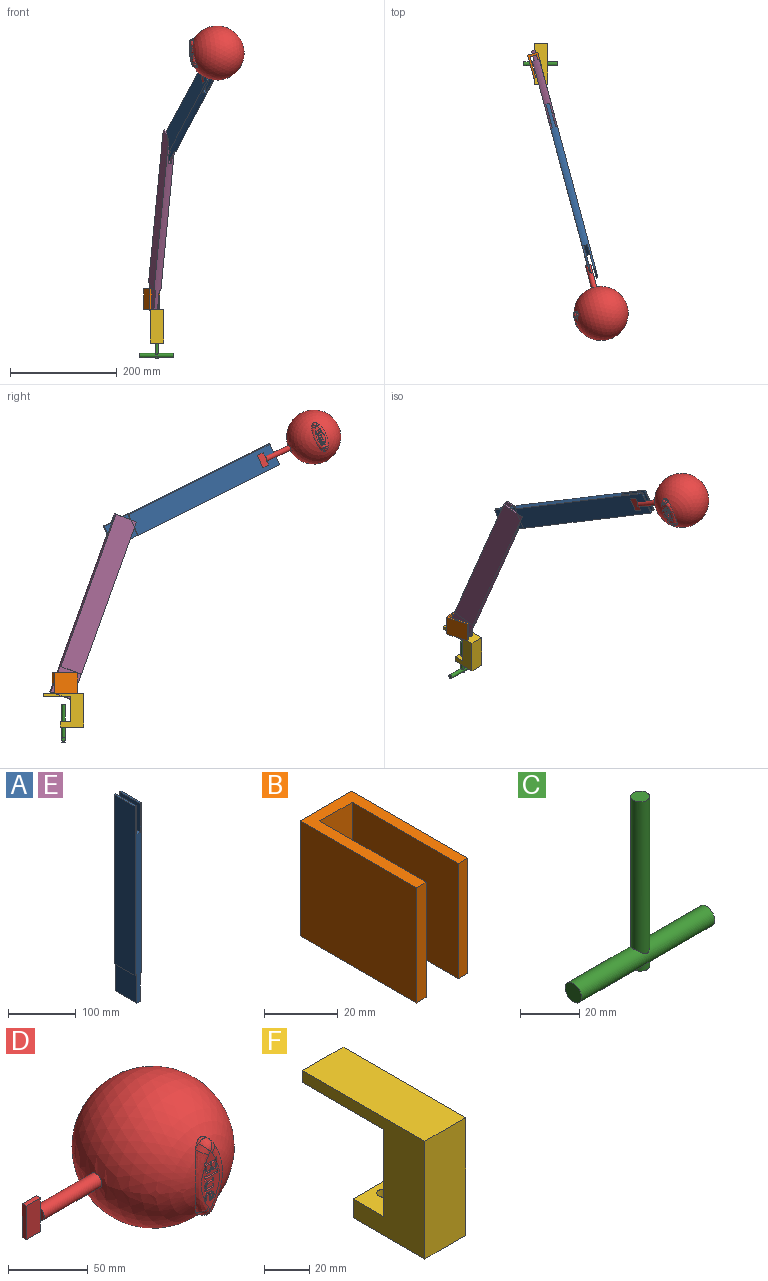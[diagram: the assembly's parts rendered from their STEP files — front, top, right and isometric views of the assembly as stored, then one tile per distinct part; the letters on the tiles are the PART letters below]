
ASSEMBLY  parts=6 mates=5
PART A: 14 faces, bbox 13.3x44.5x355.6 mm
  f0: plane 304.8x42.43mm, normal (-1,0,0), area 12932.3mm2, adj f1,f3,f6,f12
  f1: cylinder r=22.23mm len=355.6mm, axis (0,0,-1), area 4102.5mm2, adj f0,f2,f4,f5,f6,f7,f8,f9
  f2: plane 304.8x42.43mm, normal (1,0,0), area 12931.6mm2, adj f1,f3,f5,f10
  f3: cylinder r=22.23mm len=355.6mm, axis (0,0,-1), area 4102.5mm2, adj f0,f2,f4,f5,f6,f7,f8,f9
  f4: plane 44.45x6.85mm, normal (0,0,-1), area 303.3mm2, adj f1,f3,f11,f13
  f5: plane 43.92x3.2mm, normal (0,0,1), area 138.4mm2, adj f1,f2,f3,f9
  f6: plane 43.92x3.2mm, normal (0,0,1), area 138.5mm2, adj f0,f1,f3,f8
  f7: plane 44.45x6.85mm, normal (0,0,1), area 303.4mm2, adj f1,f3,f8,f9
  f8: plane 50.8x43.92mm, normal (1,0,0), area 2231.1mm2, adj f1,f3,f6,f7
  f9: plane 50.8x43.92mm, normal (-1,0,0), area 2231mm2, adj f1,f3,f5,f7
  f10: plane 43.92x3.2mm, normal (0,0,-1), area 138.6mm2, adj f1,f2,f3,f11
  f11: plane 50.8x43.92mm, normal (1,0,0), area 2231.1mm2, adj f1,f3,f4,f10
  f12: plane 43.92x3.2mm, normal (0,0,-1), area 138.4mm2, adj f0,f1,f3,f13
  f13: plane 50.8x43.92mm, normal (-1,0,0), area 2231.1mm2, adj f1,f3,f4,f12
PART B: 10 faces, bbox 19.8x44.5x38.1 mm
  f0: plane 38.1x3.72mm, normal (0,-1,0), area 141.8mm2, adj f1,f7,f8,f9
  f1: plane 44.45x38.1mm, normal (1,0,0), area 1693.5mm2, adj f0,f2,f8,f9
  f2: plane 38.1x19.78mm, normal (0,1,0), area 753.8mm2, adj f1,f3,f8,f9
  f3: plane 44.45x38.1mm, normal (-1,0,0), area 1693.5mm2, adj f2,f4,f8,f9
  f4: plane 38.1x3.77mm, normal (0,-1,0), area 143.7mm2, adj f3,f5,f8,f9
  f5: plane 40.62x38.1mm, normal (1,0,0), area 1547.5mm2, adj f4,f6,f8,f9
  f6: plane 38.1x12.29mm, normal (0,-1,0), area 468.3mm2, adj f5,f7,f8,f9
  f7: plane 40.62x38.1mm, normal (-1,0,0), area 1547.5mm2, adj f0,f6,f8,f9
  f8: plane 44.45x19.78mm, normal (0,0,1), area 380.2mm2, adj f0,f1,f2,f3,f4,f5,f6,f7
  f9: plane 44.45x19.78mm, normal (0,0,-1), area 380.2mm2, adj f0,f1,f2,f3,f4,f5,f6,f7
PART C: 7 faces, bbox 63.5x7.7x69.9 mm
  f0: cylinder r=3.17mm len=6.35mm, axis (0,0,1), area 33.7mm2, adj f1,f2
  f1: plane 6.35x6.35mm, normal (0,0,-1), area 31.7mm2, adj f0
  f2: cylinder r=3.83mm len=63.5mm, axis (-1,0,0), area 1458.5mm2, adj f0,f3,f4,f6
  f3: plane 7.67x7.67mm, normal (1,0,0), area 46.2mm2, adj f2
  f4: plane 7.67x7.67mm, normal (-1,0,0), area 46.2mm2, adj f2
  f5: plane 6.35x6.35mm, normal (0,0,1), area 31.7mm2, adj f6
  f6: cylinder r=3.17mm len=63.13mm, axis (0,0,1), area 1238.2mm2, adj f2,f5
PART D: 115 faces, bbox 165.2x101.7x101.7 mm
  f0: plane 35.77x16.03mm, normal (0,-1,0), area 275.1mm2, adj f2,f3,f17,f19,f35,f36,f37,f38
  f1: plane 8.58x8.06mm, normal (0,-1,0), area 40.5mm2, adj f2,f3,f20,f22,f47,f48,f50
  f2: bspline ~49.37x11.19mm, area 297mm2, adj f0,f1,f5,f17,f20,f35,f50
  f3: bspline ~49.37x11.19mm, area 294.8mm2, adj f0,f1,f5,f19,f22,f44,f45,f46
  f4: extruded ~13.82x5.21mm, area 28.3mm2, adj f5,f17,f18,f19
  f5: sphere r=50.8mm, area 31213.4mm2, adj f2,f3,f4,f7,f16
  f6: plane 9.52x3.31mm, normal (-1,0,0), area 22.9mm2, adj f7,f11
  f7: cylinder r=5.08mm len=51.05mm, axis (1,0,0), area 1629.6mm2, adj f5,f6,f8,f9,f15
  f8: plane 9.52x3.31mm, normal (-1,0,0), area 22.9mm2, adj f7,f13
  f9: plane 8.11x3.55mm, normal (1,0,0), area 28mm2, adj f7,f11,f12,f13
  f10: plane 12.7x3.55mm, normal (0,0,-1), area 45.1mm2, adj f11,f13,f14,f15
  f11: plane 25.75x12.7mm, normal (0,-1,0), area 327mm2, adj f6,f9,f10,f12,f14,f15
  f12: plane 12.7x3.55mm, normal (0,0,1), area 45.1mm2, adj f9,f11,f13,f14
  f13: plane 25.75x12.7mm, normal (0,1,0), area 327mm2, adj f8,f9,f10,f12,f14,f15
  f14: plane 25.75x3.55mm, normal (-1,0,0), area 91.4mm2, adj f10,f11,f12,f13
  f15: plane 8.11x3.55mm, normal (1,0,0), area 28mm2, adj f7,f10,f11,f13
  f16: extruded ~13.82x5.21mm, area 28.3mm2, adj f5,f20,f21,f22
  f17: bspline ~7.54x7.51mm, area 36.2mm2, adj f0,f2,f4,f18
  f18: bspline ~8.4x6.57mm, area 37.3mm2, adj f4,f17,f19
  f19: bspline ~7.92x7.76mm, area 36.4mm2, adj f0,f3,f4,f18
  f20: bspline ~7.66x7.66mm, area 36.3mm2, adj f1,f2,f16,f21
  f21: bspline ~8.4x6.57mm, area 37.4mm2, adj f16,f20,f22
  f22: bspline ~7.54x7.51mm, area 36.3mm2, adj f1,f3,f16,f21
  f23: plane 5.08x2.4mm, normal (-1,0,0), area 12.2mm2, adj f24,f51,f52,f112
  f24: plane 5.08x3.39mm, normal (0,0,1), area 17.2mm2, adj f23,f25,f52,f112
  f25: plane 5.08x2.03mm, normal (1,0,0), area 10.3mm2, adj f24,f26,f52,f112
  f26: extruded ~5.08x1.56mm, area 8.4mm2, adj f25,f27,f52,f112
  f27: extruded ~5.08x1.29mm, area 7.4mm2, adj f26,f28,f52,f112
  f28: extruded ~5.08x1.21mm, area 6.8mm2, adj f27,f51,f52,f112
  f29: plane 5.08x3.86mm, normal (0,0,1), area 19.6mm2, adj f30,f49,f52,f113
  f30: plane 5.08x2.7mm, normal (1,0,0), area 13.7mm2, adj f29,f31,f52,f113
  f31: extruded ~5.08x1.4mm, area 7.8mm2, adj f30,f32,f52,f113
  f32: extruded ~5.08x1.47mm, area 8mm2, adj f31,f33,f52,f113
  f33: extruded ~5.08x1.38mm, area 7.8mm2, adj f32,f34,f52,f113
  f34: extruded ~5.08x1.53mm, area 8.3mm2, adj f33,f49,f52,f113
  f35: plane 5.13x5.1mm, normal (1,0,0), area 25.9mm2, adj f0,f2,f36,f50,f52
  f36: extruded ~5.08x2.57mm, area 13.9mm2, adj f0,f35,f37,f52
  f37: extruded ~5.08x2.23mm, area 12.7mm2, adj f0,f36,f38,f52
  f38: extruded ~5.08x1.71mm, area 9.3mm2, adj f0,f37,f39,f52
  f39: extruded ~5.08x1.51mm, area 9.3mm2, adj f0,f38,f40,f52
  f40: extruded ~5.08x1.19mm, area 7.4mm2, adj f0,f39,f41,f52
  f41: extruded ~5.08x1.27mm, area 7mm2, adj f0,f40,f42,f52
  f42: extruded ~5.08x2.15mm, area 12.4mm2, adj f0,f41,f43,f52
  f43: extruded ~5.08x2.6mm, area 13.9mm2, adj f0,f42,f44,f52
  f44: plane 5.17x4.75mm, normal (-1,0,0), area 23.4mm2, adj f0,f3,f43,f45,f52
  f45: plane 5.04x0.93mm, normal (0,0,-1), area 4.6mm2, adj f3,f44,f46,f52
  f46: plane 5.09x1.2mm, normal (0.99,0,-0.17), area 6.1mm2, adj f3,f45,f47,f52
  f47: plane 8.37x5.08mm, normal (0,0,-1), area 42.5mm2, adj f1,f3,f46,f48,f52
  f48: plane 5.08x1.19mm, normal (-0.99,0,-0.17), area 6.1mm2, adj f1,f47,f50,f52
  f49: plane 5.08x2.48mm, normal (-1,0,0), area 12.6mm2, adj f29,f34,f52,f113
  f50: plane 5.08x0.92mm, normal (0,0,-1), area 4.7mm2, adj f1,f2,f35,f48,f52
  f51: extruded ~5.08x1.25mm, area 6.9mm2, adj f23,f28,f52,f112
  f52: plane 10.62x8.62mm, normal (0,-1,0), area 44.3mm2, adj f23,f24,f25,f26,f27,f28,f29,f30
  f53: plane 5.08x0.93mm, normal (0,0,-1), area 4.7mm2, adj f0,f54,f62,f63
  f54: plane 5.08x1.19mm, normal (0.99,0,-0.17), area 6.1mm2, adj f0,f53,f55,f63
  f55: plane 9.13x5.08mm, normal (0,0,-1), area 46.4mm2, adj f0,f54,f56,f63
  f56: plane 5.08x1.19mm, normal (-0.99,0,-0.17), area 6.1mm2, adj f0,f55,f57,f63
  f57: plane 5.08x0.92mm, normal (0,0,-1), area 4.7mm2, adj f0,f56,f58,f63
  f58: plane 5.08x3.81mm, normal (1,0,0), area 19.4mm2, adj f0,f57,f59,f63
  f59: plane 5.08x0.92mm, normal (0,0,1), area 4.7mm2, adj f0,f58,f60,f63
  f60: plane 5.08x1.19mm, normal (-0.99,0,0.17), area 6.1mm2, adj f0,f59,f61,f63
  f61: plane 10.26x5.08mm, normal (0,0,1), area 52.1mm2, adj f0,f60,f62,f63
  f62: plane 5.08x2.63mm, normal (-1,0,0), area 13.3mm2, adj f0,f53,f61,f63
  f63: plane 11.38x3.81mm, normal (0,-1,0), area 20mm2, adj f53,f54,f55,f56,f57,f58,f59,f60
  f64: extruded ~5.08x0.98mm, area 7mm2, adj f0,f65,f85,f86
  f65: plane 5.08x1.17mm, normal (0.08,0,-1), area 5.9mm2, adj f0,f64,f66,f86
  f66: plane 5.08x2.19mm, normal (1,0,0), area 11.1mm2, adj f0,f65,f67,f86
  f67: plane 5.08x0.92mm, normal (0,0,1), area 4.7mm2, adj f0,f66,f68,f86
  f68: plane 5.08x0.9mm, normal (-0.98,0,0.22), area 4.7mm2, adj f0,f67,f69,f86
  f69: plane 6.77x5.08mm, normal (0,0,1), area 34.4mm2, adj f0,f68,f70,f86
  f70: plane 5.08x2.5mm, normal (-1,0,0), area 12.7mm2, adj f0,f69,f71,f86
  f71: plane 5.08x0.93mm, normal (0,0,-1), area 4.7mm2, adj f0,f70,f72,f86
  f72: plane 5.08x1.06mm, normal (0.98,0,-0.19), area 5.5mm2, adj f0,f71,f73,f86
  f73: plane 5.08x4.56mm, normal (0,0,-1), area 23.2mm2, adj f0,f72,f74,f86
  f74: extruded ~5.08x0.88mm, area 6mm2, adj f0,f73,f75,f86
  f75: extruded ~5.08x1.27mm, area 6.7mm2, adj f0,f74,f76,f86
  f76: extruded ~5.08x1.16mm, area 6.6mm2, adj f0,f75,f77,f86
  f77: extruded ~5.08x1.74mm, area 9.2mm2, adj f0,f76,f78,f86
  f78: plane 5.08x4.67mm, normal (0,0,1), area 23.7mm2, adj f0,f77,f79,f86
  f79: plane 5.08x2.34mm, normal (-1,0,0), area 11.9mm2, adj f0,f78,f80,f86
  f80: plane 5.08x0.93mm, normal (0,0,-1), area 4.7mm2, adj f0,f79,f81,f86
  f81: plane 5.08x0.91mm, normal (0.98,0,-0.22), area 4.7mm2, adj f0,f80,f82,f86
  f82: plane 5.08x3.52mm, normal (0,0,-1), area 17.9mm2, adj f0,f81,f83,f86
  f83: extruded ~5.08x2.57mm, area 13.8mm2, adj f0,f82,f84,f86
  f84: extruded ~5.08x2.01mm, area 11.4mm2, adj f0,f83,f85,f86
  f85: extruded ~5.08x1.35mm, area 7.2mm2, adj f0,f64,f84,f86
  f86: plane 8.24x8.05mm, normal (0,-1,0), area 28.6mm2, adj f64,f65,f66,f67,f68,f69,f70,f71
  f87: extruded ~5.08x1.23mm, area 7.2mm2, adj f88,f110,f111,f114
  f88: extruded ~5.08x1.34mm, area 7.7mm2, adj f87,f89,f111,f114
  f89: extruded ~5.08x1.42mm, area 7.7mm2, adj f88,f90,f111,f114
  f90: plane 5.08x0.19mm, normal (0,0,-1), area 1mm2, adj f89,f91,f111,f114
  f91: plane 5.08x3.64mm, normal (-1,0,0), area 18.5mm2, adj f90,f92,f111,f114
  f92: plane 5.08x0.04mm, normal (-0.4,0,0.92), area 0.2mm2, adj f91,f110,f111,f114
  f93: extruded ~5.08x2.62mm, area 14.9mm2, adj f0,f94,f109,f111
  f94: extruded ~5.08x1.68mm, area 8.7mm2, adj f0,f93,f95,f111
  f95: extruded ~5.08x1.12mm, area 6.7mm2, adj f0,f94,f96,f111
  f96: plane 5.08x0.93mm, normal (-0.52,0,0.86), area 5.5mm2, adj f0,f95,f97,f111
  f97: extruded ~5.08x0.95mm, area 5.7mm2, adj f0,f96,f98,f111
  f98: extruded ~5.08x1.28mm, area 6.6mm2, adj f0,f97,f99,f111
  f99: extruded ~5.08x1.55mm, area 9.1mm2, adj f0,f98,f100,f111
  f100: extruded ~5.08x1.87mm, area 10.1mm2, adj f0,f99,f101,f111
  f101: plane 5.08x0.04mm, normal (0.53,0,0.85), area 0.2mm2, adj f0,f100,f102,f111
  f102: plane 5.12x5.08mm, normal (1,0,0), area 26mm2, adj f0,f101,f103,f111
  f103: plane 5.08x0.9mm, normal (0,0,1), area 4.6mm2, adj f0,f102,f104,f111
  f104: extruded ~5.08x2.57mm, area 14mm2, adj f0,f103,f105,f111
  f105: extruded ~5.08x2.41mm, area 13.6mm2, adj f0,f104,f106,f111
  f106: extruded ~5.08x2.37mm, area 13.8mm2, adj f0,f105,f107,f111
  f107: extruded ~5.08x2.8mm, area 15.5mm2, adj f0,f106,f108,f111
  f108: plane 5.08x0.32mm, normal (0,0,-1), area 1.6mm2, adj f0,f107,f109,f111
  f109: extruded ~5.08x2.85mm, area 15.7mm2, adj f0,f93,f108,f111
  f110: extruded ~5.08x1.53mm, area 8.5mm2, adj f87,f92,f111,f114
  f111: plane 8.19x6.61mm, normal (0,-1,0), area 27.4mm2, adj f87,f88,f89,f90,f91,f92,f93,f94
  f112: plane 4.13x3.39mm, normal (0,-1,0), area 12.8mm2, adj f23,f24,f25,f26,f27,f28,f51
  f113: plane 4.55x3.86mm, normal (0,-1,0), area 16.2mm2, adj f29,f30,f31,f32,f33,f34,f49
  f114: plane 3.66x2.17mm, normal (0,-1,0), area 6.3mm2, adj f87,f88,f89,f90,f91,f92,f110
PART E: same geometry as A
PART F: 11 faces, bbox 25.4x76.2x63.5 mm
  f0: plane 44.45x25.4mm, normal (0,0,-1), area 1097.4mm2, adj f1,f2,f5,f9,f10
  f1: plane 76.2x63.5mm, normal (1,0,0), area 2129mm2, adj f0,f3,f4,f5,f6,f7,f8,f10
  f2: plane 76.2x63.5mm, normal (-1,0,0), area 2129mm2, adj f0,f3,f4,f5,f6,f7,f8,f10
  f3: plane 25.4x19.05mm, normal (0,0,1), area 452.2mm2, adj f1,f2,f8,f9,f10
  f4: plane 76.2x25.4mm, normal (0,0,1), area 1935.5mm2, adj f1,f2,f5,f6
  f5: plane 63.5x25.4mm, normal (0,-1,0), area 1612.9mm2, adj f0,f1,f2,f4
  f6: plane 25.4x6.35mm, normal (0,1,0), area 161.3mm2, adj f1,f2,f4,f7
  f7: plane 50.8x25.4mm, normal (0,0,-1), area 1290.3mm2, adj f1,f2,f6,f8
  f8: plane 46.99x25.4mm, normal (0,1,0), area 1193.5mm2, adj f1,f2,f3,f7
  f9: cylinder r=3.17mm len=10.16mm, axis (0,0,-1), area 202.7mm2, adj f0,f3
  f10: plane 25.4x10.16mm, normal (0,1,0), area 258.1mm2, adj f0,f1,f2,f3
PLACE A rot(axis=(0.97,0.13,0.2),65.8deg) t=(5.22,-23.61,387.42)mm
PLACE B rot(axis=(0,0,1),15deg) t=(-28.6,92,58.21)mm
PLACE C t=(-9.57,97.3,65.2)mm
PLACE D rot(axis=(-0.2,-0.26,-0.95),78.1deg) t=(103.25,-409.55,570.32)mm
PLACE E rot(axis=(0.8,0.11,0.59),25.3deg) t=(-19.33,68.01,86.73)mm
PLACE F t=(-9.57,97.3,58.21)mm fixed
MATE cylindrical C.f0 <-> F.f9  axis (0,0,1) through (-9.57,59.2,36.62)mm
MATE revolute B.f9 <-> F.f9  axis (0,0,-1) through (-9.57,59.2,89.96)mm
MATE revolute A.f11 <-> E.f9  axis (0.97,0.26,0) through (14.94,-46.65,394.53)mm
MATE revolute B.f7 <-> E.f11  axis (-0.97,-0.26,0) through (-12.67,56.39,109.01)mm
MATE revolute D.f13 <-> A.f8  axis (0.97,0.26,0) through (79.4,-313.67,526.79)mm
